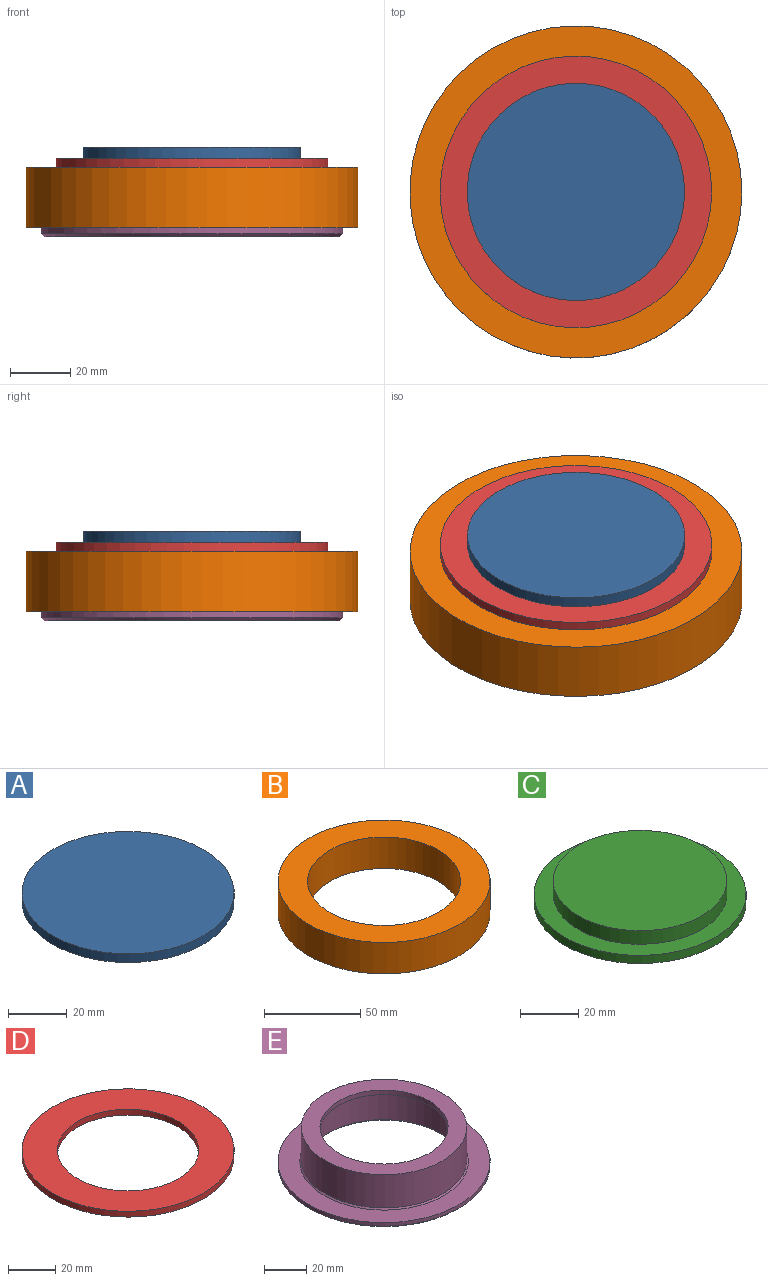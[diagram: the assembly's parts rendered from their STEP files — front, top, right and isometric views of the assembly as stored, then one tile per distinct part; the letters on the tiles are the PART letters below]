
ASSEMBLY  parts=5 mates=8
PART A: 3 faces, bbox 72x72x3.6 mm
  f0: cylinder r=36mm len=72mm, axis (0,0,-1), area 814.3mm2, adj f1,f2
  f1: plane 72x72mm, normal (0,0,1), area 4071.5mm2, adj f0
  f2: plane 72x72mm, normal (0,0,-1), area 4071.5mm2, adj f0
PART B: 4 faces, bbox 110x110x20 mm
  f0: cylinder r=39.7mm len=79.41mm, axis (0,0,-1), area 4977mm2, adj f2,f3
  f1: cylinder r=55mm len=110mm, axis (0,0,-1), area 6894.2mm2, adj f2,f3
  f2: plane 110x110mm, normal (0,0,1), area 4550.6mm2, adj f0,f1
  f3: plane 110x110mm, normal (0,0,-1), area 4550.6mm2, adj f0,f1
PART C: 5 faces, bbox 72.8x72.8x9.1 mm
  f0: cylinder r=36.4mm len=72.8mm, axis (0,0,-1), area 784.5mm2, adj f1,f2
  f1: plane 72.8x72.8mm, normal (0,0,1), area 1370.8mm2, adj f0,f3
  f2: plane 72.8x72.8mm, normal (0,0,-1), area 4162.5mm2, adj f0
  f3: cylinder r=29.81mm len=59.62mm, axis (0,0,-1), area 1067.6mm2, adj f1,f4
  f4: plane 59.62x59.62mm, normal (0,0,1), area 2791.7mm2, adj f3
PART D: 4 faces, bbox 90x90x3 mm
  f0: cylinder r=30mm len=60mm, axis (0,0,-1), area 565.5mm2, adj f2,f3
  f1: cylinder r=45mm len=90mm, axis (0,0,-1), area 848.2mm2, adj f2,f3
  f2: plane 90x90mm, normal (0,0,1), area 3534.3mm2, adj f0,f1
  f3: plane 90x90mm, normal (0,0,-1), area 3534.3mm2, adj f0,f1
PART E: 12 faces, bbox 100x100x22.9 mm
  f0: cylinder r=37mm len=74mm, axis (0,0,-1), area 4010.2mm2, adj f8,f11
  f1: cylinder r=50mm len=100mm, axis (0,0,-1), area 628.3mm2, adj f2,f9
  f2: plane 100x100mm, normal (0,0,1), area 2890.1mm2, adj f1,f10
  f3: plane 98x98mm, normal (0,0,-1), area 3006.5mm2, adj f8,f9
  f4: cylinder r=39mm len=78mm, axis (0,0,-1), area 4680.3mm2, adj f7,f10
  f5: plane 70x70mm, normal (0,0,-1), area 983.2mm2, adj f6,f11
  f6: cylinder r=30.2mm len=60.4mm, axis (0,0,-1), area 493.4mm2, adj f5,f7
  f7: plane 78x78mm, normal (0,0,1), area 1913.1mm2, adj f4,f6
  f8: cone r=38mm half-angle=45deg, axis (0,0,-1), area 333.2mm2, adj f0,f3
  f9: cone r=50mm half-angle=45deg, axis (0,0,1), area 439.8mm2, adj f1,f3
  f10: cone r=39mm half-angle=45deg, axis (0,0,-1), area 262.4mm2, adj f2,f4
  f11: cone r=37mm half-angle=45deg, axis (0,0,-1), area 639.8mm2, adj f0,f5
PLACE A t=(33.09,-102.19,3.62)mm
PLACE B t=(33.09,-102.19,-19.33)mm
PLACE C t=(33.09,-102.19,-5.51)mm
PLACE D t=(33.09,-102.19,0.62)mm
PLACE E t=(33.09,-102.19,-22.33)mm
MATE planar D.f1 <-> A.f0  axis (0,0,1) through (33.09,-102.19,3.62)mm
MATE planar B.f1 <-> D.f1  axis (0,0,1) through (33.09,-102.19,0.62)mm
MATE cylindrical A.f0 <-> C.f3  axis (0,0,-1) through (33.09,-102.19,3.62)mm
MATE cylindrical B.f1 <-> C.f0  axis (0,0,1) through (33.09,-102.19,0.62)mm
MATE planar A.f0 <-> C.f3  axis (0,0,-1) through (33.09,-102.19,3.62)mm
MATE cylindrical C.f0 <-> E.f4  axis (0,0,-1) through (33.09,-102.19,-5.51)mm
MATE cylindrical A.f0 <-> D.f1  axis (0,0,1) through (33.09,-102.19,7.22)mm
MATE planar E.f0 <-> C.f0  axis (0,0,-1) through (33.09,-102.19,-2.08)mm
